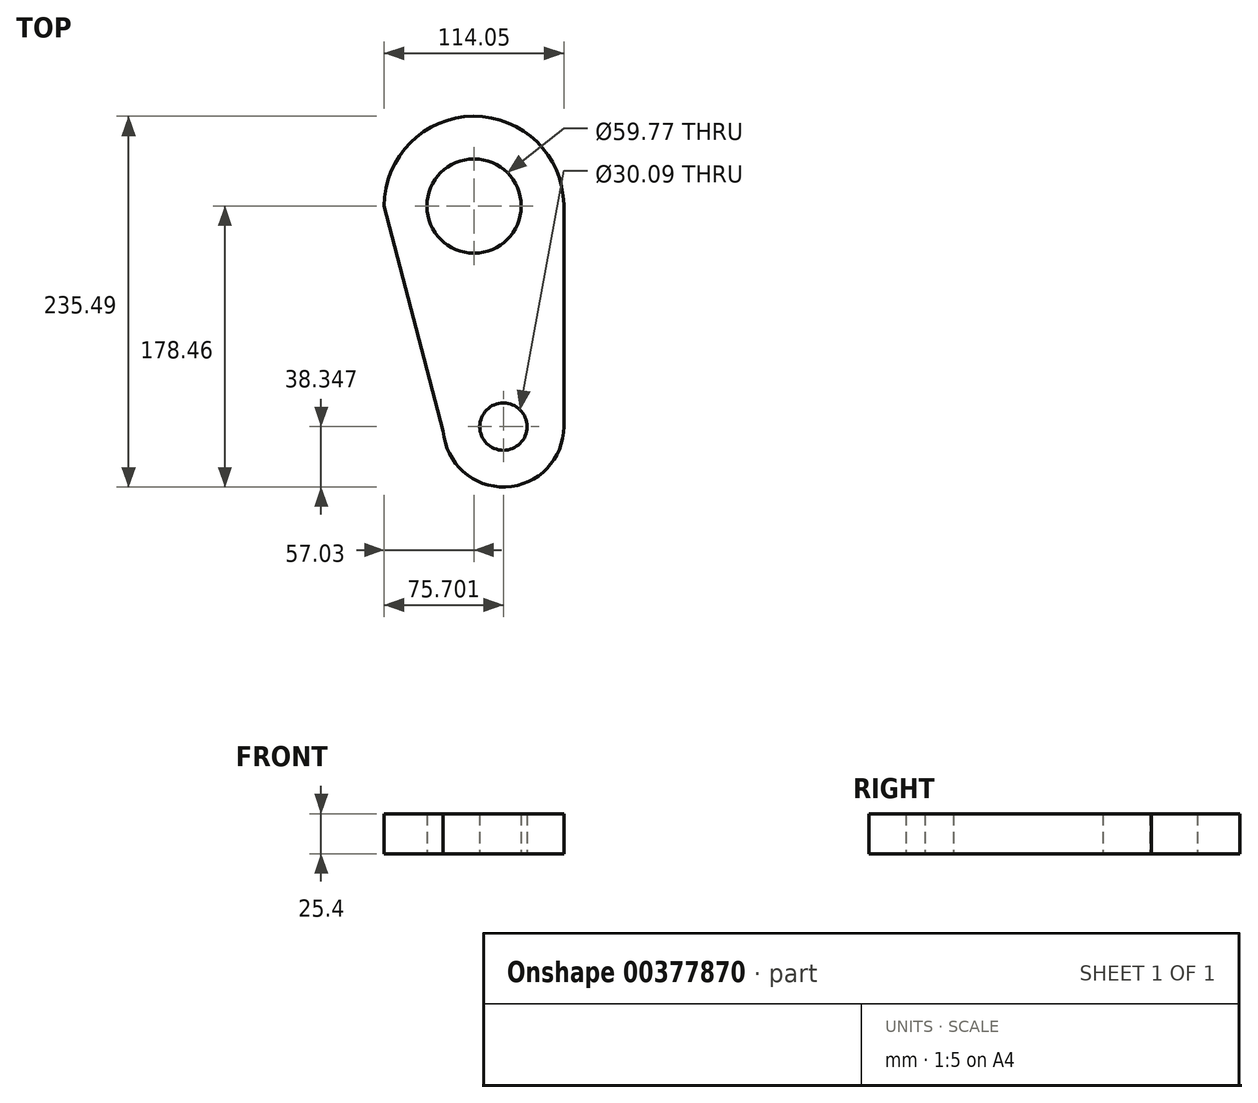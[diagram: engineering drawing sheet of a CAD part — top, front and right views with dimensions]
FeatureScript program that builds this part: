
annotation { "Feature Type Name" : "Feature", "Feature Type Description" : "" }
export const myFeature = defineFeature(function(context is Context, id is Id, definition is map)
    precondition{}
    {
        {
            var Q0;
            Q0=qCreatedBy(makeId("Top.planeOp"),FACE);
            var sketch = newSketch(context, id + "F0", { "sketchPlane" : qUnion([Q0])});
            skArc(sketch, "E0", {"start": v(-57.03, 0) * mm, "mid": v(-0.43, 57.02) * mm, "end": v(57.02, 0.87) * mm});
            skLineSegment(sketch, "E1", {"start": v(-57.03, 0) * mm, "end": v(-19.57, -143.04) * mm});
            skLineSegment(sketch, "E2", {"start": v(57.02, 0.87) * mm, "end": v(57.02, -140.11) * mm});
            skArc(sketch, "E3", {"start": v(57.02, -140.11) * mm, "mid": v(20.14, -178.43) * mm, "end": v(-19.57, -143.04) * mm});
            skCircle(sketch, "E4", {"center": v(0, 0) * mm, "radius": 29.88 * mm});
            skCircle(sketch, "E5", {"center": v(18.67, -140.11) * mm, "radius": 15.04 * mm});
            skSolve(sketch);
        }
        {
            var Q0;
            Q0 = qSketchRegion(id + "F0", true);
            extrude(context, id + "F1", {"entities" : qUnion([Q0]), "depth" : 25.4 * mm});
        }
    });
